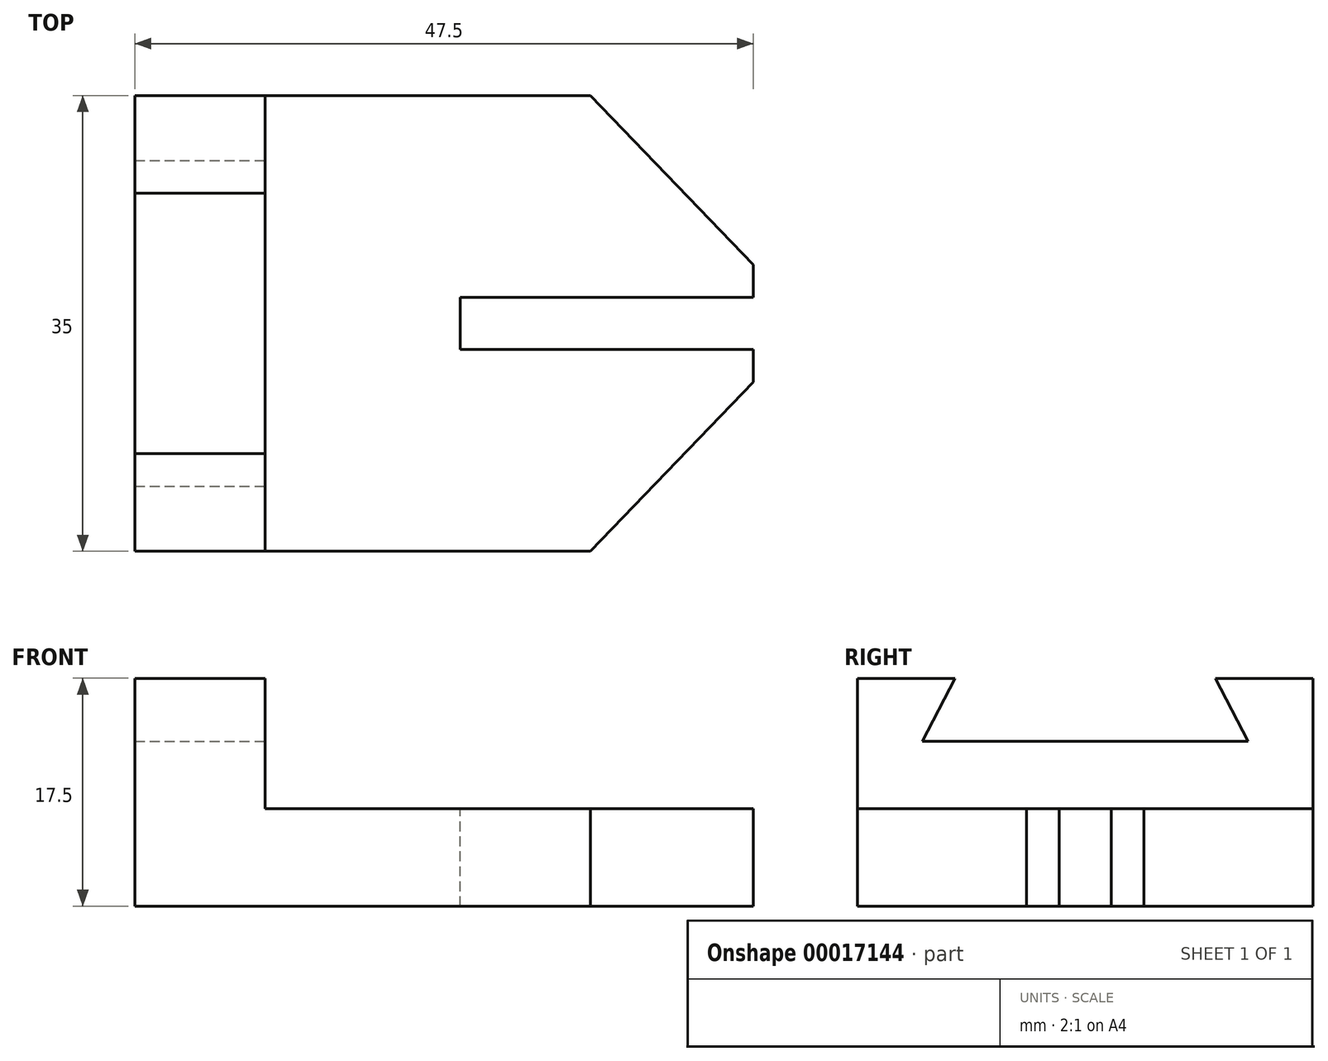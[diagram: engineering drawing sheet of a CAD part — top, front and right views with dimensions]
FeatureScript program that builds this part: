
annotation { "Feature Type Name" : "Feature", "Feature Type Description" : "" }
export const myFeature = defineFeature(function(context is Context, id is Id, definition is map)
    precondition{}
    {
        {
            var Q0;
            Q0=qCreatedBy(makeId("Front.planeOp"),FACE);
            var sketch = newSketch(context, id + "F0", { "sketchPlane" : qUnion([Q0])});
            skLineSegment(sketch, "E0", {"start": v(-14.7, -17.81) * mm, "end": v(-14.7, -0.31) * mm});
            skLineSegment(sketch, "E1", {"start": v(-14.7, -17.81) * mm, "end": v(32.8, -17.81) * mm});
            skLineSegment(sketch, "E2", {"start": v(-14.7, -0.31) * mm, "end": v(-4.7, -0.31) * mm});
            skLineSegment(sketch, "E3", {"start": v(-4.7, -0.31) * mm, "end": v(-4.7, -10.31) * mm});
            skLineSegment(sketch, "E4", {"start": v(-4.7, -10.31) * mm, "end": v(32.8, -10.31) * mm});
            skLineSegment(sketch, "E5", {"start": v(32.8, -10.31) * mm, "end": v(32.8, -17.81) * mm});
            skSolve(sketch);
        }
        {
            var Q0;
            Q0=makeQuery(id+"F0.imprint","IMPRINT",FACE,{"disambiguationData":[TD([[makeQuery(id+"F0.imprint","IMPRINT",EDGE,{"derivedFrom":sQuery(id+"F0.wireOp",EDGE,"E0")}),-1.0]])]});
            extrude(context, id + "F1", {"entities" : qUnion([Q0]), "depth" : 35 * mm});
        }
        {
            var Q0;
            Q0=makeQuery(id+"F1.opExtrude","SWEPT_FACE",FACE,{"disambiguationData":[OSD([sQuery(id+"F0.wireOp",EDGE,"E4")])]});
            var sketch = newSketch(context, id + "F2", { "sketchPlane" : qUnion([Q0])});
            skLineSegment(sketch, "E6", {"start": v(32.8, -15.5) * mm, "end": v(10.3, -15.5) * mm});
            skLineSegment(sketch, "E7", {"start": v(10.3, -15.5) * mm, "end": v(10.3, -19.5) * mm});
            skLineSegment(sketch, "E8", {"start": v(10.3, -19.5) * mm, "end": v(32.8, -19.5) * mm});
            skLineSegment(sketch, "E9", {"start": v(32.8, -15.5) * mm, "end": v(32.8, 0) * mm});
            skLineSegment(sketch, "E10", {"start": v(32.8, -19.5) * mm, "end": v(32.8, -35) * mm});
            skSolve(sketch);
        }
        {
            var Q0;
            {var subQ2=sQuery(id+"F2.wireOp",EDGE,"E6");Q0=makeQuery(id+"F2.imprint","IMPRINT",FACE,{"disambiguationData":[TD([[makeQuery(id+"F2.imprint","IMPRINT",EDGE,{"derivedFrom":subQ2}),1.0]])]});}
            extrude(context, id + "F3", {"entities" : qUnion([Q0]), "operationType" : NewBodyOperationType.REMOVE, "endBound" : BoundingType.THROUGH_ALL, "oppositeDirection" : true, "depth" : 25 * mm});
        }
        {
            var Q0;
            Q0=makeQuery(id+"F1.opExtrude","SWEPT_FACE",FACE,{"disambiguationData":[OSD([sQuery(id+"F0.wireOp",EDGE,"E4")])]});
            var sketch = newSketch(context, id + "F4", { "sketchPlane" : qUnion([Q0])});
            skLineSegment(sketch, "E11", {"start": v(32.8, -35) * mm, "end": v(32.8, -22) * mm});
            skLineSegment(sketch, "E12", {"start": v(32.8, -35) * mm, "end": v(20.3, -35) * mm});
            skLineSegment(sketch, "E13", {"start": v(20.3, -35) * mm, "end": v(32.8, -22) * mm});
            skLineSegment(sketch, "E14", {"start": v(32.8, 0) * mm, "end": v(32.8, -13) * mm});
            skLineSegment(sketch, "E15", {"start": v(32.8, 0) * mm, "end": v(20.3, 0) * mm});
            skLineSegment(sketch, "E16", {"start": v(20.3, 0) * mm, "end": v(32.8, -13) * mm});
            skSolve(sketch);
        }
        {
            var Q0;
            Q0=makeQuery(id+"F4.imprint","IMPRINT",FACE,{"disambiguationData":[TD([[makeQuery(id+"F4.imprint","IMPRINT",EDGE,{"derivedFrom":sQuery(id+"F4.wireOp",EDGE,"E14")}),1.0]])]});
            var Q1;
            Q1=makeQuery(id+"F4.imprint","IMPRINT",FACE,{"disambiguationData":[TD([[makeQuery(id+"F4.imprint","IMPRINT",EDGE,{"derivedFrom":sQuery(id+"F4.wireOp",EDGE,"E11")}),1.0]])]});
            extrude(context, id + "F5", {"entities" : qUnion([Q0, Q1]), "operationType" : NewBodyOperationType.REMOVE, "endBound" : BoundingType.THROUGH_ALL, "oppositeDirection" : true, "depth" : 25 * mm});
        }
        {
            var Q0;
            Q0=makeQuery(id+"F1.opExtrude","SWEPT_FACE",FACE,{"disambiguationData":[OSD([sQuery(id+"F0.wireOp",EDGE,"E3")])]});
            var sketch = newSketch(context, id + "F6", { "sketchPlane" : qUnion([Q0])});
            skLineSegment(sketch, "E17", {"start": v(-27.5, -0.31) * mm, "end": v(-30, -5.16) * mm});
            skLineSegment(sketch, "E18", {"start": v(-30, -5.16) * mm, "end": v(-5, -5.16) * mm});
            skLineSegment(sketch, "E19", {"start": v(-5, -5.16) * mm, "end": v(-7.5, -0.31) * mm});
            skLineSegment(sketch, "E20", {"start": v(-27.5, -0.31) * mm, "end": v(-7.5, -0.31) * mm});
            skSolve(sketch);
        }
        {
            var Q0;
            Q0=makeQuery(id+"F6.imprint","IMPRINT",FACE,{"disambiguationData":[TD([[makeQuery(id+"F6.imprint","IMPRINT",EDGE,{"derivedFrom":sQuery(id+"F6.wireOp",EDGE,"E17")}),1.0]])]});
            extrude(context, id + "F7", {"entities" : qUnion([Q0]), "operationType" : NewBodyOperationType.REMOVE, "endBound" : BoundingType.THROUGH_ALL, "oppositeDirection" : true, "depth" : 25 * mm});
        }
    });
